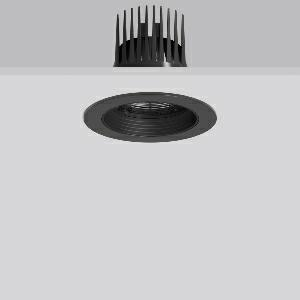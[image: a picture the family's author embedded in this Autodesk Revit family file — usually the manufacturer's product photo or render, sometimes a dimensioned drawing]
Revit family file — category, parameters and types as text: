
# Revit family: heledon_maxi_e_901760_003_2_76_0ef5
name_source: partatom
category: Lighting Fixtures
units: mm (PartAtom-declared; Revit-internal decimal feet)

## family parameters
Cut with Voids When Loaded = No
Host = Face
Light Source = No
Part Type = Normal
Room Calculation Point = No
Round Connector Dimension = Use Diameter
Shared = No

## types (1)
- HELEDON maxi E (1 x LED Modul 927, 2650 lm, 2700)
    Apparent Load = 25 VA
    Approval mark = CE
    CIE Flux Codes = 97 100 100 100 100
    Color Rendering = 92
    Color Temperature = 2700
    Default Elevation = 1800 mm
    Description = Series: HELEDON maxi
Round recessed downlight. Housing: die-cast aluminium, powder-coated. Black plastic ring and recessed LED to prevent glare from the side. Optical assembly with lens made of plastic (polycarbonate) for the best homogeneous light distribution - can be changed without tools. Best colour rendering index Ra>90. Suitable for Recessed ceiling mounting. Installation without tools thanks to spring fastening system. Including separate LED converter with connecting cable 600 mm.High quality converter without flickering and stroboscopic effect. Through-wiring box (5 pole) available as accessory. The following accessories can be mounted without use of tools: interchangeable lenses, decorative glasses, honeycomb louvre, clear and frosted diffusers, white interchangeable plastic ring. 
Colour: deep black, matt (RAL 9005)
Diameter: 162 mm
Height: 3 mm
Cut-out diameter: 152 mm
Recess height: 200 mm
Luminaire: recess height: 135 mm
Lamp: LED
Socket: without socket
Colour temperature: 2700K
Colour rendering index (CRI): 92
System power: 25 W
Rated luminous flux: 2650 lm
Luminous efficiency: 106 lm/W
Control gear: Converter, dimmable, DALI
Protection class: II
Type of protection: IP 20
    Height = 0 mm  [stored 0 ft]
    Lamp = 1 x LED Modul 927
    Lamp Light Flux = 2650 lm
    Lamp count = 1
    Length = 162 mm
    Lifetime = 50000 h
    Luminous efficacy = 106 lm/W
    Manufacturer = RZB
    ModVariant = No
    Model = 901760.003.2.76
    Mounting Place = Ceiling
    Mounting Type = Recessed
    Number of Poles = 1
    OnlyDefault = Yes
    Power Factor = 1
    Product Name = HELEDON maxi E
    Product group = Recessed downlights
    ProductGroupID = 402
    Protection Class = Protection class II
    Protection Degree = IP 20
    RLX_Detail_Level = 1
    RLX_Emergency_Light_Flux = 0 lm
    RLX_Emergency_Type = 0
    RLX_Emergency_Type_DB = No
    RlxData = <blob elided: 122329 chars, md5=ee91de62>
    Socket = socket
    Standby Power = 0 W
    System Light Flux = 2650 lm
    System Power = 25 W
    Type Comments = Product without accessories
    Type Image = 901663.003.jpg
    URL = http://relux.com
    VarID = ---
    Voltage = 230 V
    Voltage Range = 220-240 V
    Weight = 0.00 kg
    Width = 0 mm  [stored 0 ft]

note: [stored X ft] marks values corroborated as IEEE doubles in the binary element streams (Revit-internal decimal feet)

## geometry (parser evidence)
native form markers: Blend x4, Sweep x11
no freeform markers — native parametric forms only
